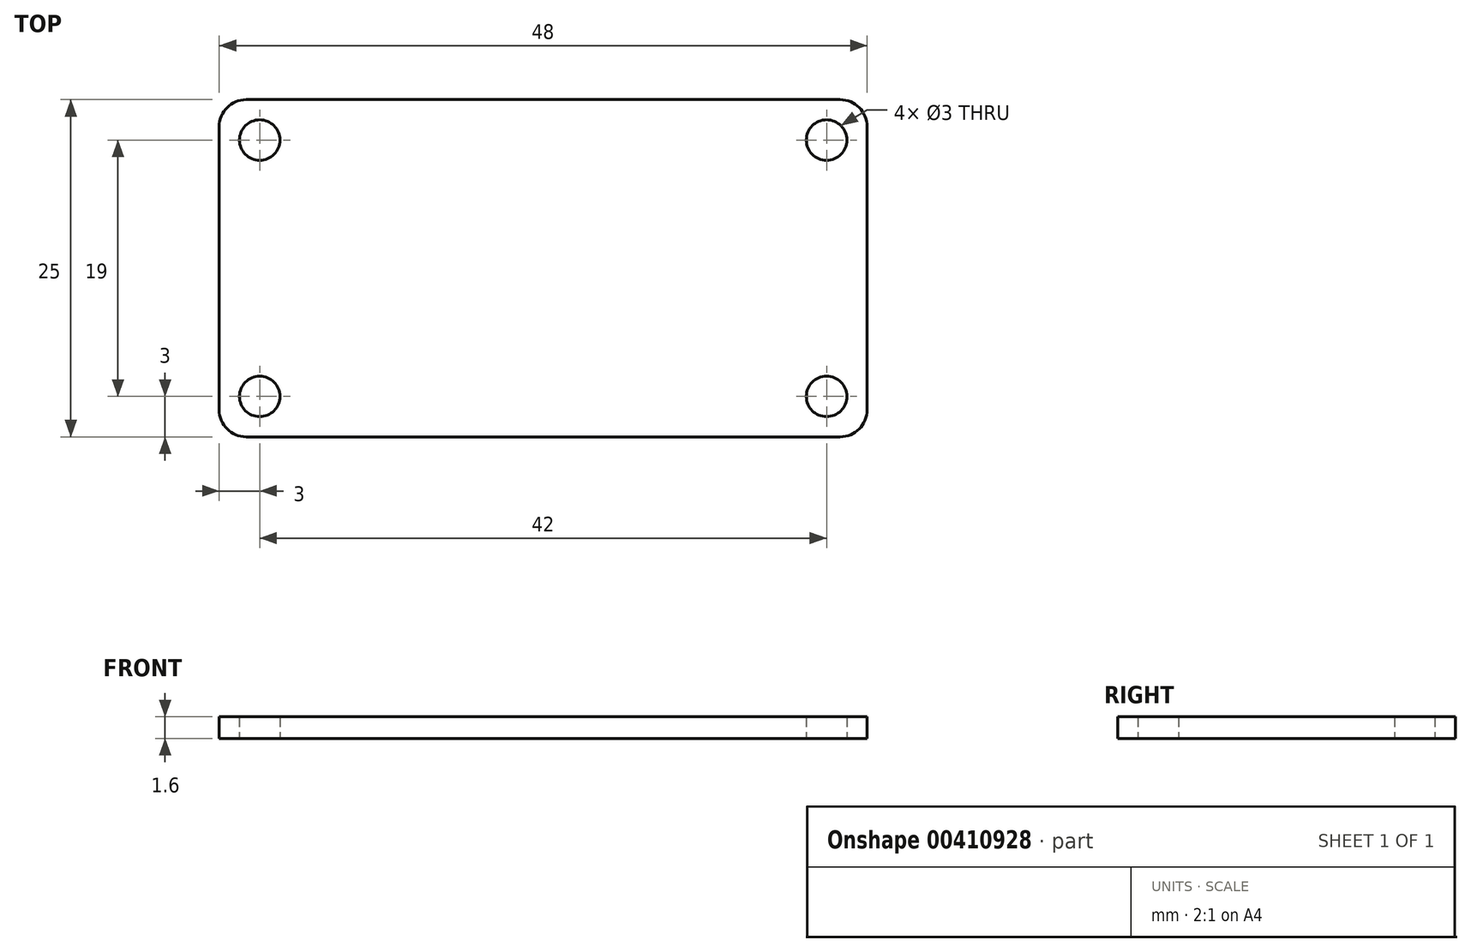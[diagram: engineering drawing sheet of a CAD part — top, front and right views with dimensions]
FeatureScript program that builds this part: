
annotation { "Feature Type Name" : "Feature", "Feature Type Description" : "" }
export const myFeature = defineFeature(function(context is Context, id is Id, definition is map)
    precondition{}
    {
        {
            var Q0;
            Q0=qCreatedBy(makeId("Top.planeOp"),FACE);
            var sketch = newSketch(context, id + "F0", { "sketchPlane" : qUnion([Q0])});
            skLineSegment(sketch, "E0.bottom", {"start": v(0, 0) * mm, "end": v(48, 0) * mm});
            skLineSegment(sketch, "E0.top", {"start": v(0, 25) * mm, "end": v(48, 25) * mm});
            skLineSegment(sketch, "E0.left", {"start": v(0, 0) * mm, "end": v(0, 25) * mm});
            skLineSegment(sketch, "E0.right", {"start": v(48, 0) * mm, "end": v(48, 25) * mm});
            skCircle(sketch, "E1", {"center": v(3, 22) * mm, "radius": 1.5 * mm});
            skLineSegment(sketch, "E2", {"start": v(0, 12.5) * mm, "end": v(48, 12.5) * mm, "construction": true});
            skLineSegment(sketch, "E3", {"start": v(24, 25) * mm, "end": v(24, 0) * mm, "construction": true});
            skCircle(sketch, "E4.MirrorC", {"center": v(45, 22) * mm, "radius": 1.5 * mm});
            skCircle(sketch, "E5.MirrorC", {"center": v(3, 3) * mm, "radius": 1.5 * mm});
            skCircle(sketch, "E6.MirrorC", {"center": v(45, 3) * mm, "radius": 1.5 * mm});
            skSolve(sketch);
        }
        {
            var Q0;
            Q0 = qSketchRegion(id + "F0", true);
            extrude(context, id + "F1", {"entities" : qUnion([Q0]), "depth" : 1.6 * mm});
        }
        {
            var Q0;
            Q0=makeQuery(id+"F1.opExtrude","SWEPT_EDGE",EDGE,{"disambiguationData":[OSD([sQuery(id+"F0.wireOp",EDGE,"E0.bottom"),sQuery(id+"F0.wireOp",EDGE,"E0.right")])]});
            var Q1;
            Q1=makeQuery(id+"F1.opExtrude","SWEPT_EDGE",EDGE,{"disambiguationData":[OSD([sQuery(id+"F0.wireOp",EDGE,"E0.top"),sQuery(id+"F0.wireOp",EDGE,"E0.right")])]});
            var Q2;
            Q2=makeQuery(id+"F1.opExtrude","SWEPT_EDGE",EDGE,{"disambiguationData":[OSD([sQuery(id+"F0.wireOp",EDGE,"E0.top"),sQuery(id+"F0.wireOp",EDGE,"E0.left")])]});
            var Q3;
            Q3=makeQuery(id+"F1.opExtrude","SWEPT_EDGE",EDGE,{"disambiguationData":[OSD([sQuery(id+"F0.wireOp",EDGE,"E0.bottom"),sQuery(id+"F0.wireOp",EDGE,"E0.left")])]});
            fillet(context, id + "F2", {"entities" : qUnion([Q0, Q1, Q2, Q3]), "radius" : 2 * mm, "tangentPropagation" : true, "allowEdgeOverflow" : false});
        }
    });
